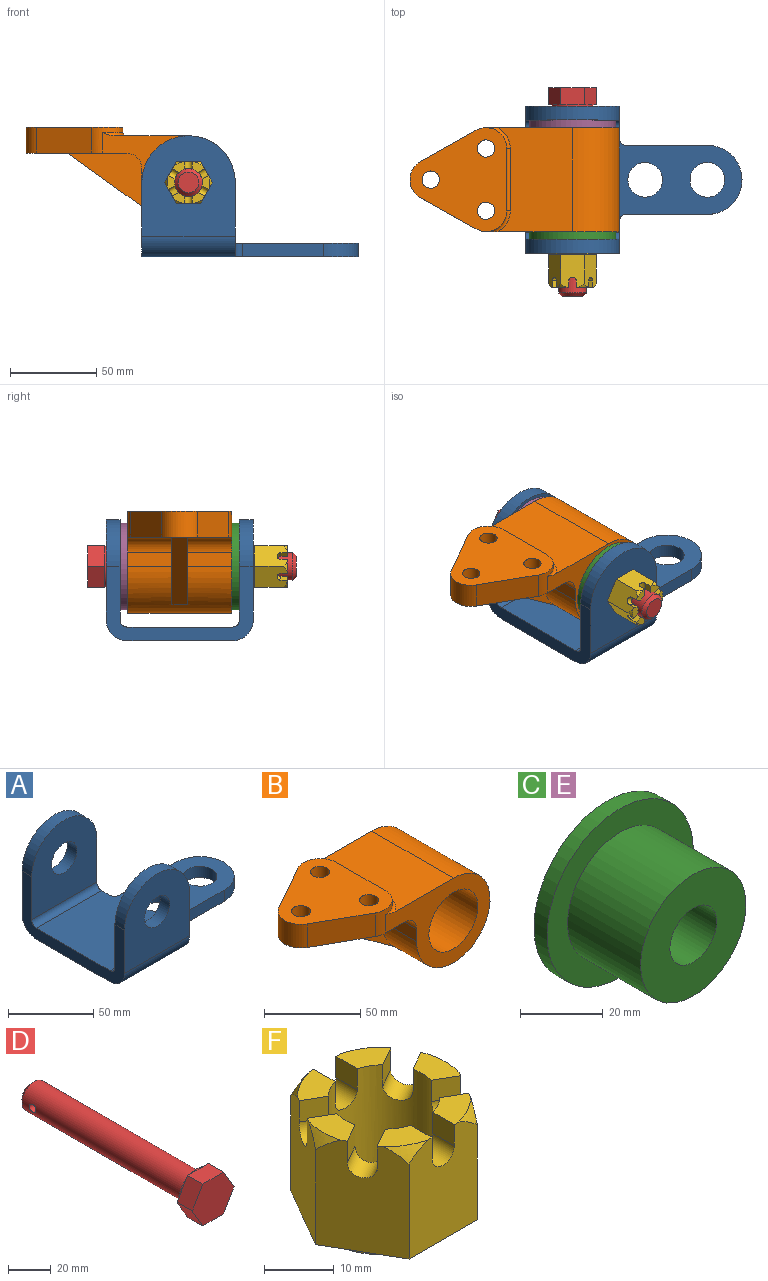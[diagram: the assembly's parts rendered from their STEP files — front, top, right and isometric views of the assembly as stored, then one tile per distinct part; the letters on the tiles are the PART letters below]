
ASSEMBLY  parts=6 mates=5
PART A: 24 faces, bbox 125x85x70 mm
  f0: plane 125x61mm, normal (0,0,1), area 5340.9mm2, adj f1,f2,f3,f4,f6,f8,f9,f10
  f1: plane 47x8mm, normal (0,-1,0), area 376mm2, adj f0,f2,f11,f23
  f2: cylinder r=20mm len=40mm, axis (0,0,-1), area 502.7mm2, adj f0,f1,f3,f11
  f3: plane 47x8mm, normal (0,1,0), area 376mm2, adj f0,f2,f11,f22
  f4: plane 43x18.5mm, normal (1,0,0), area 400.5mm2, adj f0,f5,f11,f15,f17,f19,f20,f22
  f5: plane 58x54mm, normal (0,1,0), area 2472.7mm2, adj f4,f6,f15,f16,f19
  f6: plane 85x43mm, normal (-1,0,0), area 1185.1mm2, adj f0,f5,f7,f11,f12,f13,f15,f17
  f7: plane 58x54mm, normal (0,-1,0), area 2472.7mm2, adj f6,f10,f13,f14,f18
  f8: cylinder r=10mm len=20mm, axis (0,0,-1), area 502.7mm2, adj f0,f11
  f9: cylinder r=10mm len=20mm, axis (0,0,-1), area 502.7mm2, adj f0,f11
  f10: plane 43x18.5mm, normal (1,0,0), area 400.5mm2, adj f0,f7,f11,f12,f13,f18,f21,f23
  f11: plane 125x61mm, normal (0,0,-1), area 5340.9mm2, adj f1,f2,f3,f4,f6,f8,f9,f10
  f12: plane 58x54mm, normal (0,1,0), area 2472.7mm2, adj f6,f10,f13,f14,f21
  f13: cylinder r=27mm len=54mm, axis (0,-1,0), area 678.6mm2, adj f6,f7,f10,f12
  f14: cylinder r=10.5mm len=21mm, axis (0,-1,0), area 527.8mm2, adj f7,f12
  f15: cylinder r=27mm len=54mm, axis (0,1,0), area 678.6mm2, adj f4,f5,f6,f17
  f16: cylinder r=10.5mm len=21mm, axis (0,1,0), area 527.8mm2, adj f5,f17
  f17: plane 58x54mm, normal (0,-1,0), area 2472.7mm2, adj f4,f6,f15,f16,f20
  f18: cylinder r=12mm len=54mm, axis (1,0,0), area 1017.9mm2, adj f6,f7,f10,f11
  f19: cylinder r=12mm len=54mm, axis (-1,0,0), area 1017.9mm2, adj f4,f5,f6,f11
  f20: cylinder r=4mm len=54mm, axis (1,0,0), area 339.3mm2, adj f0,f4,f6,f17
  f21: cylinder r=4mm len=54mm, axis (-1,0,0), area 339.3mm2, adj f0,f6,f10,f12
  f22: cylinder r=4mm len=8mm, axis (0,0,1), area 50.3mm2, adj f0,f3,f4,f11
  f23: cylinder r=4mm len=8mm, axis (0,0,1), area 50.3mm2, adj f0,f1,f10,f11
PART B: 26 faces, bbox 121x69.4x59 mm
  f0: plane 25.5x8mm, normal (-1,0,0), area 204mm2, adj f2,f3,f9,f25
  f1: plane 60x58mm, normal (0,0,-1), area 1981.7mm2, adj f2,f4,f8,f9,f10,f11,f12,f13
  f2: cylinder r=9mm len=25.5mm, axis (0,1,0), area 360.5mm2, adj f0,f1,f9,f25
  f3: cylinder r=27mm len=60mm, axis (0,1,0), area 7403.6mm2, adj f0,f5,f6,f8,f9,f23,f24,f25
  f4: cylinder r=9mm len=25.5mm, axis (0,1,0), area 360.5mm2, adj f1,f5,f8,f24
  f5: plane 25.5x8mm, normal (-1,0,0), area 204mm2, adj f3,f4,f8,f24
  f6: plane 60x42.79mm, normal (0,0,1), area 2207.6mm2, adj f3,f8,f9,f20,f21,f22
  f7: cylinder r=18mm len=60mm, axis (0,1,0), area 6785.8mm2, adj f8,f9
  f8: plane 77x56mm, normal (0,-1,0), area 1681.7mm2, adj f1,f3,f4,f5,f6,f7,f16,f20
  f9: plane 77x56mm, normal (0,1,0), area 1681.7mm2, adj f0,f1,f2,f3,f6,f7,f12,f22
  f10: cylinder r=5mm len=15mm, axis (0,0,1), area 471.2mm2, adj f1,f18
  f11: cylinder r=5mm len=15mm, axis (0,0,1), area 471.2mm2, adj f1,f18
  f12: cylinder r=12mm len=17.88mm, axis (0,0,1), area 148.8mm2, adj f1,f9,f13,f18,f19,f22
  f13: plane 32x18mm, normal (-0.49,0.87,0), area 550.7mm2, adj f1,f12,f14,f18
  f14: cylinder r=12mm len=20.92mm, axis (0,0,1), area 381mm2, adj f1,f13,f15,f18
  f15: plane 32x18mm, normal (-0.49,-0.87,0), area 550.7mm2, adj f1,f14,f16,f18
  f16: cylinder r=12mm len=17.88mm, axis (0,0,1), area 148.8mm2, adj f1,f8,f15,f18,f19,f20
  f17: cylinder r=5mm len=15mm, axis (0,0,1), area 471.2mm2, adj f1,f18
  f18: plane 60x56mm, normal (0,0,1), area 2105.9mm2, adj f10,f11,f12,f13,f14,f15,f16,f17
  f19: plane 36x3mm, normal (1,0,0), area 108mm2, adj f12,f16,f18,f21
  f20: torus R=14mm, axis (0,0,-1), area 50.8mm2, adj f6,f8,f16,f21
  f21: cylinder r=2mm len=36mm, axis (0,-1,0), area 113.1mm2, adj f6,f19,f20,f22
  f22: torus R=14mm, axis (0,0,-1), area 50.8mm2, adj f6,f9,f12,f21
  f23: plane 54.26x38.94mm, normal (-0.58,0,-0.81), area 601mm2, adj f1,f3,f24,f25
  f24: plane 54.26x38.94mm, normal (0,-1,0), area 674.5mm2, adj f1,f3,f4,f5,f23
  f25: plane 54.26x38.94mm, normal (0,1,0), area 674.5mm2, adj f0,f1,f2,f3,f23
PART C: 6 faces, bbox 50x29.5x50 mm
  f0: cylinder r=25mm len=50mm, axis (0,-1,0), area 706.9mm2, adj f1,f2
  f1: plane 50x50mm, normal (0,1,0), area 1762.4mm2, adj f0,f3
  f2: plane 50x50mm, normal (0,-1,0), area 945.6mm2, adj f0,f4
  f3: cylinder r=8mm len=29.5mm, axis (0,1,0), area 1482.8mm2, adj f1,f5
  f4: cylinder r=18mm len=36mm, axis (0,1,0), area 2827.4mm2, adj f2,f5
  f5: plane 36x36mm, normal (0,-1,0), area 816.8mm2, adj f3,f4
PART D: 19 faces, bbox 27.7x120.8x24 mm
  f0: cylinder r=8mm len=108mm, axis (0,1,0), area 5396.5mm2, adj f2,f17,f18
  f1: cylinder r=12mm len=24mm, axis (0,1,0), area 60.3mm2, adj f2,f3,f4,f5,f6,f7,f8
  f2: plane 24x24mm, normal (0,1,0), area 251.3mm2, adj f0,f1
  f3: plane 10.39x6mm, normal (0,1,0), area 7.7mm2, adj f1,f13,f14
  f4: plane 10.39x6mm, normal (0,1,0), area 7.7mm2, adj f1,f9,f14
  f5: plane 12x3.46mm, normal (0,1,0), area 7.7mm2, adj f1,f9,f10
  f6: plane 10.39x6mm, normal (0,1,0), area 7.7mm2, adj f1,f10,f11
  f7: plane 10.39x6mm, normal (0,1,0), area 7.7mm2, adj f1,f11,f12
  f8: plane 12x3.46mm, normal (0,1,0), area 7.7mm2, adj f1,f12,f13
  f9: plane 12x10mm, normal (-0.87,0,0.5), area 138.6mm2, adj f4,f5,f10,f14,f15
  f10: plane 12x10mm, normal (-0.87,0,-0.5), area 138.6mm2, adj f5,f6,f9,f11,f15
  f11: plane 13.86x10mm, normal (0,0,-1), area 138.6mm2, adj f6,f7,f10,f12,f15
  f12: plane 12x10mm, normal (0.87,0,-0.5), area 138.6mm2, adj f7,f8,f11,f13,f15
  f13: plane 12x10mm, normal (0.87,0,0.5), area 138.6mm2, adj f3,f8,f12,f14,f15
  f14: plane 13.86x10mm, normal (0,0,1), area 138.6mm2, adj f3,f4,f9,f13,f15
  f15: plane 27.71x24mm, normal (0,-1,0), area 498.8mm2, adj f9,f10,f11,f12,f13,f14
  f16: plane 12x12mm, normal (0,1,0), area 113.1mm2, adj f17
  f17: cone r=8mm half-angle=45deg, axis (0,-1,0), area 124.4mm2, adj f0,f16
  f18: cylinder r=2.25mm len=16mm, axis (1,0,0), area 221.7mm2, adj f0
PART E: same geometry as C
PART F: 40 faces, bbox 27.7x26.8x19.8 mm
  f0: plane 8.1x4.64mm, normal (0,0,1), area 26.9mm2, adj f7,f8,f12,f22,f31,f37
  f1: plane 7.02x6.21mm, normal (0,0,1), area 26.9mm2, adj f9,f10,f12,f21,f30,f35
  f2: plane 7.02x6.21mm, normal (0,0,1), area 26.9mm2, adj f6,f7,f12,f16,f32,f38
  f3: plane 19x12mm, normal (-0.87,-0.5,0), area 231mm2, adj f4,f6,f10,f11,f13,f25,f26,f27
  f4: plane 7.02x6.21mm, normal (0,0,1), area 26.9mm2, adj f3,f6,f12,f17,f26,f39
  f5: plane 7.02x6.21mm, normal (0,0,1), area 26.9mm2, adj f8,f9,f12,f20,f23,f36
  f6: plane 19.01x13.87mm, normal (0,-1,0), area 231mm2, adj f2,f3,f4,f7,f13,f16,f17,f18
  f7: plane 19x12mm, normal (0.87,-0.5,0), area 231mm2, adj f0,f2,f6,f8,f13,f31,f32,f33
  f8: plane 19x12mm, normal (0.87,0.5,0), area 231mm2, adj f0,f5,f7,f9,f13,f22,f23,f24
  f9: plane 19.01x13.87mm, normal (0,1,0), area 231mm2, adj f1,f5,f8,f10,f13,f19,f20,f21
  f10: plane 19x12mm, normal (-0.87,0.5,0), area 231mm2, adj f1,f3,f9,f11,f13,f28,f29,f30
  f11: plane 8.1x4.64mm, normal (0,0,1), area 26.9mm2, adj f3,f10,f12,f27,f29,f34
  f12: cylinder r=8mm len=19.8mm, axis (0,0,1), area 844.4mm2, adj f0,f1,f2,f4,f5,f11,f15,f16
  f13: plane 27.71x24mm, normal (0,0,-1), area 101.2mm2, adj f3,f6,f7,f8,f9,f10,f14
  f14: cylinder r=11.25mm len=22.5mm, axis (0,0,1), area 56.5mm2, adj f13,f15
  f15: plane 22.5x22.5mm, normal (0,0,-1), area 196.5mm2, adj f12,f14
  f16: plane 4.32x3.75mm, normal (-1,0,0), area 16.2mm2, adj f2,f6,f12,f18
  f17: plane 4.32x3.75mm, normal (1,0,0), area 16.2mm2, adj f4,f6,f12,f18
  f18: cylinder r=2.25mm len=4.5mm, axis (0,-1,0), area 29.4mm2, adj f6,f12,f16,f17
  f19: cylinder r=2.25mm len=4.5mm, axis (0,-1,0), area 29.4mm2, adj f9,f12,f20,f21
  f20: plane 4.32x3.75mm, normal (-1,0,0), area 16.2mm2, adj f5,f9,f12,f19
  f21: plane 4.32x3.75mm, normal (1,0,0), area 16.2mm2, adj f1,f9,f12,f19
  f22: plane 3.75x3.74mm, normal (-0.5,0.87,0), area 16.2mm2, adj f0,f8,f12,f24
  f23: plane 3.75x3.74mm, normal (0.5,-0.87,0), area 16.2mm2, adj f5,f8,f12,f24
  f24: cylinder r=2.25mm len=6.06mm, axis (-0.87,-0.5,0), area 29.4mm2, adj f8,f12,f22,f23
  f25: cylinder r=2.25mm len=6.06mm, axis (-0.87,-0.5,0), area 29.4mm2, adj f3,f12,f26,f27
  f26: plane 3.75x3.74mm, normal (-0.5,0.87,0), area 16.2mm2, adj f3,f4,f12,f25
  f27: plane 3.75x3.74mm, normal (0.5,-0.87,0), area 16.2mm2, adj f3,f11,f12,f25
  f28: cylinder r=2.25mm len=6.06mm, axis (0.87,-0.5,0), area 29.4mm2, adj f10,f12,f29,f30
  f29: plane 3.75x3.74mm, normal (0.5,0.87,0), area 16.2mm2, adj f10,f11,f12,f28
  f30: plane 3.75x3.74mm, normal (-0.5,-0.87,0), area 16.2mm2, adj f1,f10,f12,f28
  f31: plane 3.75x3.74mm, normal (-0.5,-0.87,0), area 16.2mm2, adj f0,f7,f12,f33
  f32: plane 3.75x3.74mm, normal (0.5,0.87,0), area 16.2mm2, adj f2,f7,f12,f33
  f33: cylinder r=2.25mm len=6.06mm, axis (0.87,-0.5,0), area 29.4mm2, adj f7,f12,f31,f32
  f34: revolved ~7.27x2.34mm, area 7.8mm2, adj f3,f10,f11
  f35: revolved ~6.66x4.65mm, area 7.8mm2, adj f1,f9,f10
  f36: revolved ~6.66x4.65mm, area 7.8mm2, adj f5,f8,f9
  f37: revolved ~7.27x2.34mm, area 7.8mm2, adj f0,f7,f8
  f38: revolved ~6.66x4.65mm, area 7.8mm2, adj f2,f6,f7
  f39: revolved ~6.66x4.65mm, area 7.8mm2, adj f3,f4,f6
PLACE A at identity fixed
PLACE B t=(-27,8.21,43)mm
PLACE C rot(axis=(0,0,1),180deg) t=(-27,-21.79,43)mm
PLACE D rot(axis=(0,0,1),180deg) t=(-27,-15.49,43)mm
PLACE E t=(-27,38.21,43)mm
PLACE F rot(axis=(1,0,0),90deg) t=(-27,-35.09,43)mm
MATE cylindrical B.f3 <-> E.f0  axis (0,1,0) through (-27,38.21,43)mm
MATE cylindrical E.f0 <-> A.f15  axis (0,1,0) through (-27,42.71,43)mm
MATE planar A.f15 <-> F.f12  axis (0,-1,0) through (-27,-34.29,43)mm
MATE cylindrical F.f12 <-> A.f15  axis (0,1,0) through (-27,-34.29,43)mm
MATE cylindrical D.f0 <-> A.f13  axis (0,-1,0) through (-27,50.71,43)mm
